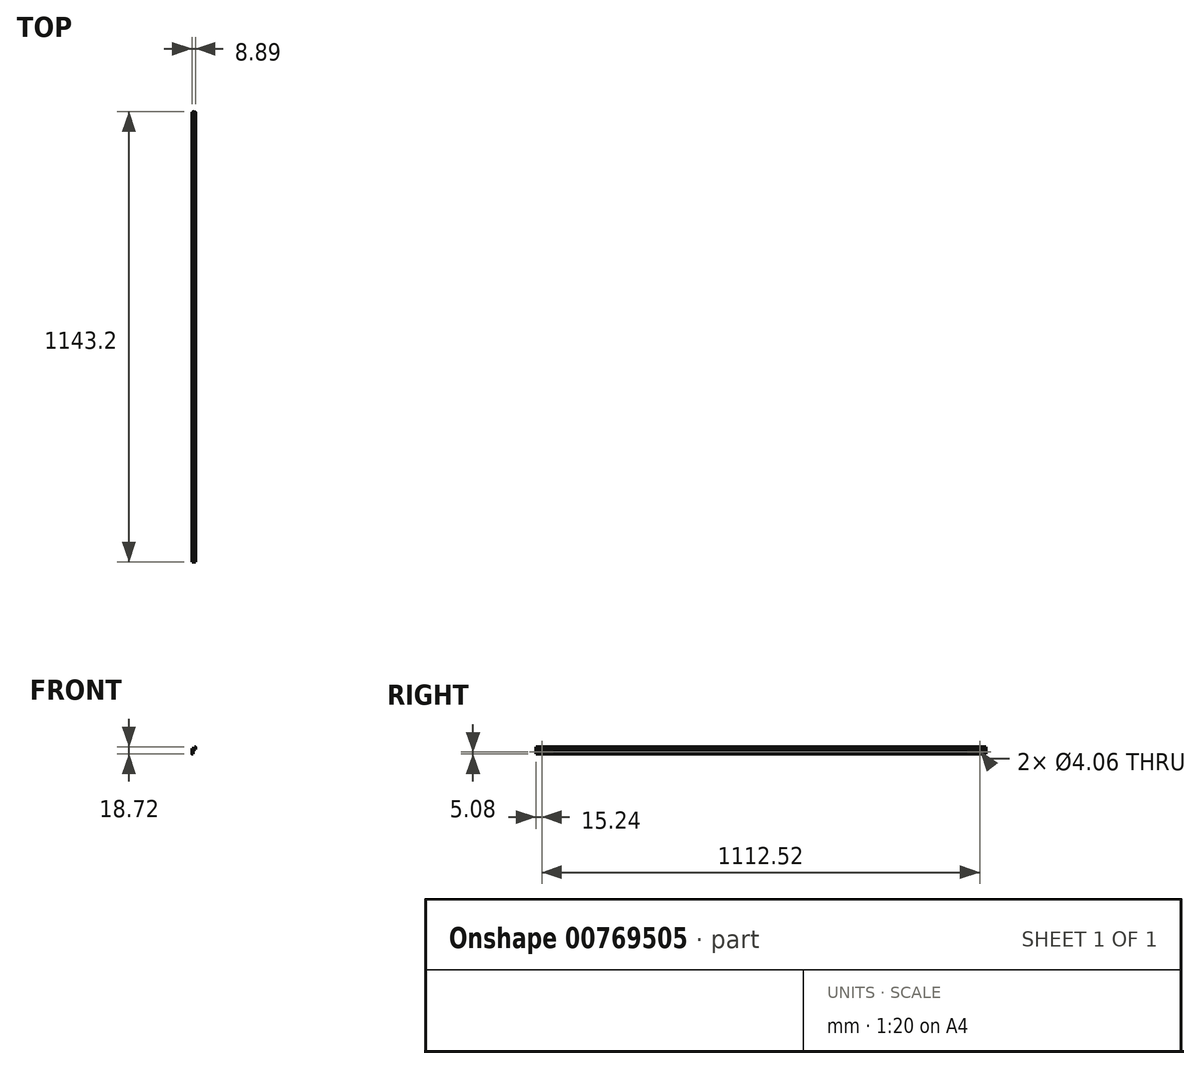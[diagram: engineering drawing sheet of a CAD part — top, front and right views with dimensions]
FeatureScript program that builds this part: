
annotation { "Feature Type Name" : "Feature", "Feature Type Description" : "" }
export const myFeature = defineFeature(function(context is Context, id is Id, definition is map)
    precondition{}
    {
        {
            var Q0;
            Q0=qCreatedBy(makeId("Front.planeOp"),FACE);
            var sketch = newSketch(context, id + "F0", { "sketchPlane" : qUnion([Q0])});
            skLineSegment(sketch, "E0.bottom", {"start": v(0, 0) * mm, "end": v(8.9, 0) * mm});
            skLineSegment(sketch, "E0.top", {"start": v(0, 18.72) * mm, "end": v(8.89, 18.72) * mm});
            skLineSegment(sketch, "E0.left", {"start": v(0, 0) * mm, "end": v(0, 18.72) * mm});
            skLineSegment(sketch, "E0.right", {"start": v(8.9, 0) * mm, "end": v(8.9, 18.72) * mm});
            skSolve(sketch);
        }
        {
            var Q0;
            Q0 = qSketchRegion(id + "F0", true);
            extrude(context, id + "F1", {"entities" : qUnion([Q0]), "depth" : 1143 * mm, "offsetDistance" : 25.4 * mm});
        }
        {
            var Q0;
            Q0=makeQuery(id+"F1.opExtrude","CAP_FACE",FACE,{"disambiguationData":[OSD([sQuery(id+"F0.wireOp",EDGE,"E0.bottom"),sQuery(id+"F0.wireOp",EDGE,"E0.top"),sQuery(id+"F0.wireOp",EDGE,"E0.left"),sQuery(id+"F0.wireOp",EDGE,"E0.right")])],"isStart":false});
            var sketch = newSketch(context, id + "F2", { "sketchPlane" : qUnion([Q0])});
            skLineSegment(sketch, "E1.bottom", {"start": v(0, 18.72) * mm, "end": v(6.35, 18.72) * mm});
            skLineSegment(sketch, "E1.top", {"start": v(0, 13.97) * mm, "end": v(6.35, 13.97) * mm});
            skLineSegment(sketch, "E1.left", {"start": v(0, 18.72) * mm, "end": v(0, 13.97) * mm});
            skLineSegment(sketch, "E1.right", {"start": v(6.35, 18.72) * mm, "end": v(6.35, 13.97) * mm});
            skPoint(sketch, "E2.oppositeSnap0", {"position": v(2.54, 0) * mm});
            skLineSegment(sketch, "E2.bottom", {"start": v(8.9, 0) * mm, "end": v(2.54, 0) * mm});
            skLineSegment(sketch, "E2.top", {"start": v(8.9, 11.43) * mm, "end": v(2.54, 11.43) * mm});
            skLineSegment(sketch, "E2.left", {"start": v(8.9, 0) * mm, "end": v(8.9, 11.43) * mm});
            skLineSegment(sketch, "E2.right", {"start": v(2.54, 0) * mm, "end": v(2.54, 11.43) * mm});
            skSolve(sketch);
        }
        {
            var Q0;
            Q0 = qSketchRegion(id + "F2", true);
            extrude(context, id + "F3", {"entities" : qUnion([Q0]), "operationType" : NewBodyOperationType.REMOVE, "endBound" : BoundingType.THROUGH_ALL, "oppositeDirection" : true, "depth" : 25.4 * mm, "offsetDistance" : 25.4 * mm});
        }
        {
            var Q0;
            Q0=makeQuery(id+"F3.boolean.opBoolean","COPY",EDGE,{"derivedFrom":makeQuery(id+"F3.opExtrude","SWEPT_EDGE",EDGE,{"disambiguationData":[OSD([sQuery(id+"F0.wireOp",EDGE,"E0.top"),sQuery(id+"F2.wireOp",EDGE,"E1.bottom"),sQuery(id+"F2.wireOp",EDGE,"E1.right")])]})});
            var Q1;
            Q1=makeQuery(id+"F1.opExtrude","SWEPT_EDGE",EDGE,{"disambiguationData":[OSD([sQuery(id+"F0.wireOp",EDGE,"E0.top"),sQuery(id+"F0.wireOp",EDGE,"E0.right")])]});
            var Q2;
            Q2=makeQuery(id+"F3.boolean.opBoolean","COPY",EDGE,{"derivedFrom":makeQuery(id+"F3.opExtrude","SWEPT_EDGE",EDGE,{"disambiguationData":[OSD([sQuery(id+"F0.wireOp",EDGE,"E0.bottom"),sQuery(id+"F2.wireOp",EDGE,"E2.bottom"),sQuery(id+"F2.wireOp",EDGE,"E2.right")])]})});
            var Q3;
            Q3=makeQuery(id+"F1.opExtrude","SWEPT_EDGE",EDGE,{"disambiguationData":[OSD([sQuery(id+"F0.wireOp",EDGE,"E0.bottom"),sQuery(id+"F0.wireOp",EDGE,"E0.left")])]});
            var Q4;
            Q4=makeQuery(id+"F3.boolean.opBoolean","COPY",EDGE,{"derivedFrom":makeQuery(id+"F3.opExtrude","SWEPT_EDGE",EDGE,{"disambiguationData":[OSD([sQuery(id+"F0.wireOp",EDGE,"E0.left"),sQuery(id+"F2.wireOp",EDGE,"E1.top"),sQuery(id+"F2.wireOp",EDGE,"E1.left")])]})});
            fillet(context, id + "F4", {"entities" : qUnion([Q0, Q1, Q2, Q3, Q4]), "radius" : 0.13 * mm, "tangentPropagation" : true, "allowEdgeOverflow" : false});
        }
        {
            var Q0;
            Q0=makeQuery(id+"F1.opExtrude","CAP_FACE",FACE,{"disambiguationData":[OSD([sQuery(id+"F0.wireOp",EDGE,"E0.bottom"),sQuery(id+"F0.wireOp",EDGE,"E0.top"),sQuery(id+"F0.wireOp",EDGE,"E0.left"),sQuery(id+"F0.wireOp",EDGE,"E0.right")])],"isStart":false});
            var sketch = newSketch(context, id + "F5", { "sketchPlane" : qUnion([Q0])});
            skLineSegment(sketch, "E3", {"start": v(3.81, 11.43) * mm, "end": v(2.54, 10.16) * mm});
            skLineSegment(sketch, "E4", {"start": v(2.54, 10.16) * mm, "end": v(2.54, 11.43) * mm});
            skLineSegment(sketch, "E5", {"start": v(2.54, 11.43) * mm, "end": v(3.81, 11.43) * mm});
            skSolve(sketch);
        }
        {
            var Q0;
            Q0=makeQuery(id+"F5.imprint","IMPRINT",FACE,{"disambiguationData":[TD([[makeQuery(id+"F5.imprint","IMPRINT",EDGE,{"derivedFrom":sQuery(id+"F5.wireOp",EDGE,"E3")}),-1.0]])]});
            extrude(context, id + "F6", {"entities" : qUnion([Q0]), "endBound" : BoundingType.THROUGH_ALL, "oppositeDirection" : true, "depth" : 25.4 * mm, "offsetDistance" : 25.4 * mm});
        }
        {
            var Q0;
            Q0=makeQuery(id+"F3.boolean.opBoolean","COPY",FACE,{"derivedFrom":makeQuery(id+"F3.opExtrude","SWEPT_FACE",FACE,{"disambiguationData":[OSD([sQuery(id+"F2.wireOp",EDGE,"E2.right")])]})});
            var sketch = newSketch(context, id + "F7", { "sketchPlane" : qUnion([Q0])});
            skCircle(sketch, "E6", {"center": v(-1127.76, 5.08) * mm, "radius": 2.03 * mm});
            skCircle(sketch, "E7", {"center": v(-15.24, 5.08) * mm, "radius": 2.03 * mm});
            skSolve(sketch);
        }
        {
            var Q0;
            Q0 = qSketchRegion(id + "F7", true);
            extrude(context, id + "F8", {"entities" : qUnion([Q0]), "operationType" : NewBodyOperationType.REMOVE, "endBound" : BoundingType.UP_TO_NEXT, "oppositeDirection" : true, "depth" : 25.4 * mm, "offsetDistance" : 25.4 * mm});
        }
    });
